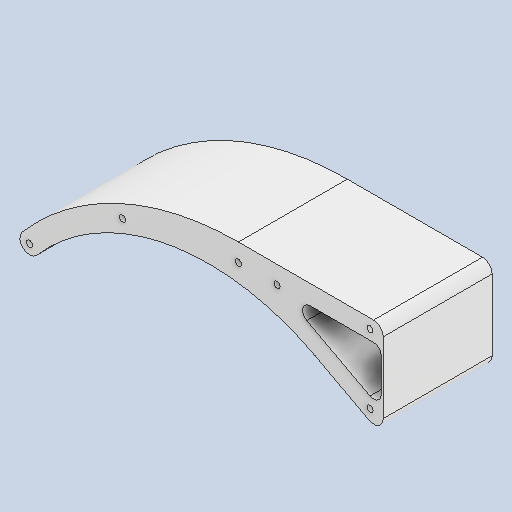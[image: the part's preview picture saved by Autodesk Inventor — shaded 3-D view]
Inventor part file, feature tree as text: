
AUTODESK INVENTOR PART (.ipt)
format: ipt  version: 2025.1 (Build 291241000, 241)  size: 169,472 bytes
history: native  units: mm
features: other x6, reference x2, sketch x1, extrude x1, fillet x1
ambient origin geometry x8: Origin, YZ Plane, XZ Plane, XY Plane, X Axis, Y Axis, Z Axis, Center Point
bodies: Body1 (feature_tree)
feature tree (11):
  other  "ソリッド1"
  sketch  "スケッチ1"
  other  "作業平面1"
  extrude  "押し出し1"  Depth=1.6mm
  fillet  "フィレット1"  Radius=1.6mm
  reference  "参照1"
  reference  "参照2"
  other  "<userpath>\Documents\Inventor\Vixen\doutai.iam"
  other  "doutai.iam"
  other  "tesaki:1"
  other  "KRS3300_scale:1"
